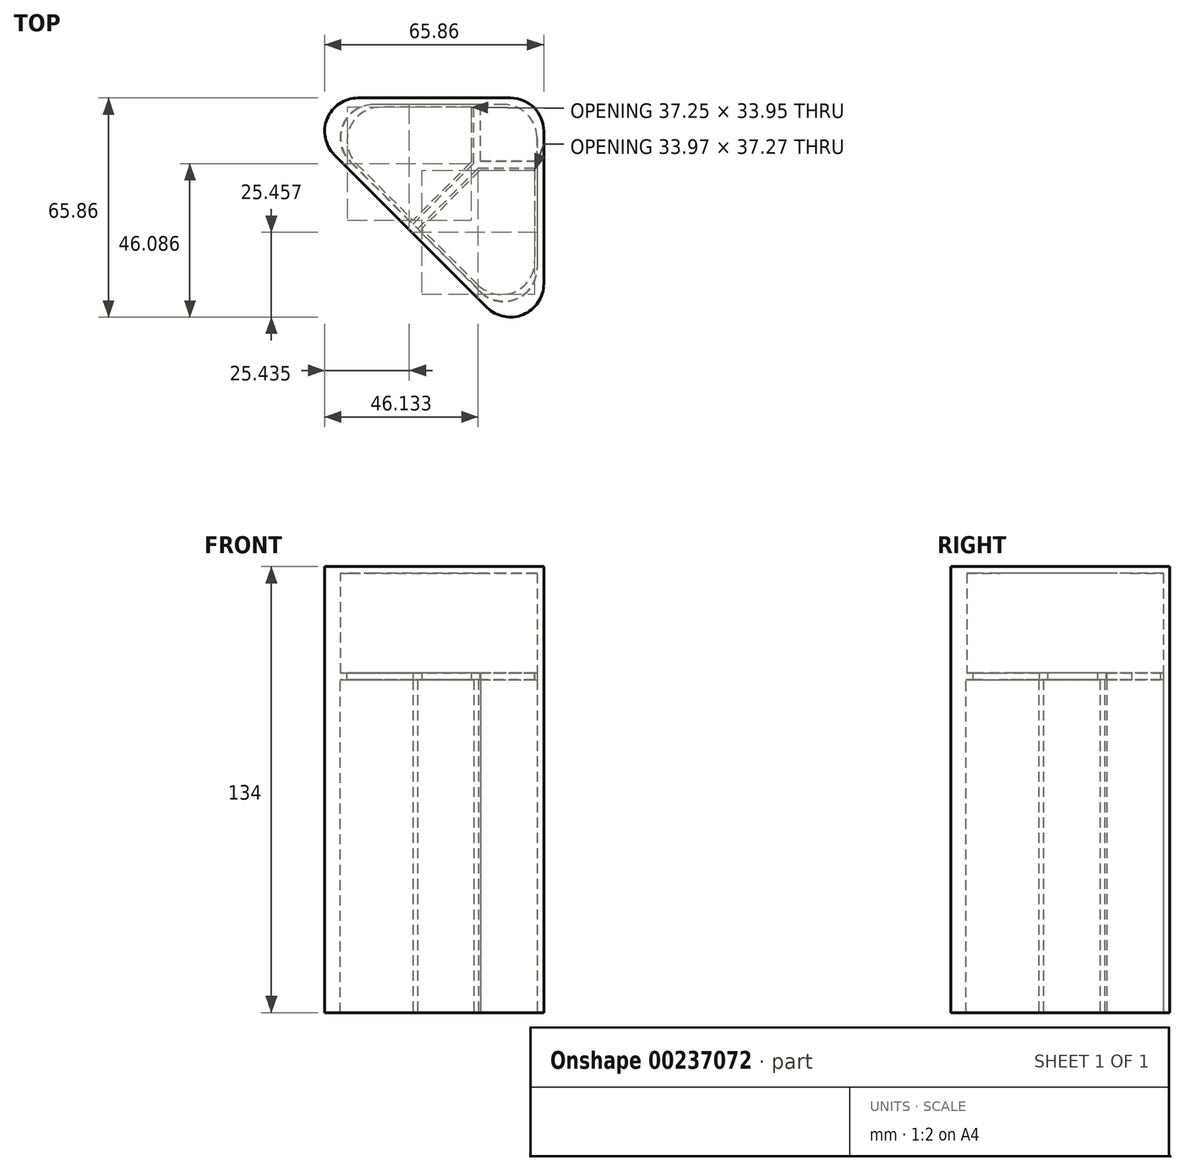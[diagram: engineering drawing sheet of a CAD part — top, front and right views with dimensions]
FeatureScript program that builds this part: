
annotation { "Feature Type Name" : "Feature", "Feature Type Description" : "" }
export const myFeature = defineFeature(function(context is Context, id is Id, definition is map)
    precondition{}
    {
        {
            var Q0;
            Q0=qCreatedBy(makeId("Top.planeOp"),FACE);
            var sketch = newSketch(context, id + "F0", { "sketchPlane" : qUnion([Q0])});
            skLineSegment(sketch, "E0.top", {"start": v(40, 40) * mm, "end": v(-40, 40) * mm});
            skLineSegment(sketch, "E0.left", {"start": v(40, -40) * mm, "end": v(40, 40) * mm});
            skPoint(sketch, "E0.middle", {"position": v(0, 0) * mm});
            skLineSegment(sketch, "E1", {"start": v(-40, 40) * mm, "end": v(40, -40) * mm});
            skPoint(sketch, "E0.bottom.end.orphan", {"position": v(-40, -40) * mm});
            skLineSegment(sketch, "E2", {"start": v(40, 40) * mm, "end": v(20, 40) * mm, "construction": true});
            skLineSegment(sketch, "E3", {"start": v(40, 40) * mm, "end": v(20, 20) * mm, "construction": true});
            skPoint(sketch, "E4.orphan", {"position": v(-20, 20) * mm});
            skPoint(sketch, "E5.orphan", {"position": v(20, -20) * mm});
            skLineSegment(sketch, "E6", {"start": v(0, 0) * mm, "end": v(-0.7, 0.7) * mm, "construction": true});
            skLineSegment(sketch, "E7", {"start": v(0.61, 2.03) * mm, "end": v(19, 20.41) * mm});
            skLineSegment(sketch, "E8", {"start": v(21, 21) * mm, "end": v(21, 38) * mm});
            skLineSegment(sketch, "E9.MirrorCS", {"start": v(19, 20.41) * mm, "end": v(19, 38) * mm});
            skPoint(sketch, "E10.start.orphan", {"position": v(20, 21.41) * mm});
            skPoint(sketch, "E11.MirrorCS.end.orphan", {"position": v(21, 20) * mm});
            skPoint(sketch, "E11.MirrorCS.start.orphan", {"position": v(40, 20) * mm});
            skLineSegment(sketch, "E12.0", {"start": v(38, 38) * mm, "end": v(21, 38) * mm});
            skLineSegment(sketch, "E13.trimOffspring", {"start": v(19, 38) * mm, "end": v(-35.36, 38) * mm});
            skLineSegment(sketch, "E14.0", {"start": v(-40.1, 39.9) * mm, "end": v(39.9, -40.1) * mm});
            skLineSegment(sketch, "E15.trimOffspring", {"start": v(-38, 38) * mm, "end": v(-38.19, 38) * mm});
            skLineSegment(sketch, "E16.trimOffspring", {"start": v(-35.36, 38) * mm, "end": v(0.61, 2.03) * mm});
            skLineSegment(sketch, "E17.trimOffspring", {"start": v(40, -37.36) * mm, "end": v(41.32, -38.68) * mm});
            skLineSegment(sketch, "E18.MirrorCS", {"start": v(38, 19) * mm, "end": v(38, -35.36) * mm});
            skLineSegment(sketch, "E19.MirrorCS", {"start": v(20.41, 19) * mm, "end": v(38, 19) * mm});
            skLineSegment(sketch, "E20.MirrorCS", {"start": v(21, 21) * mm, "end": v(38, 21) * mm});
            skLineSegment(sketch, "E21.MirrorCS", {"start": v(38, 38) * mm, "end": v(38, 21) * mm});
            skLineSegment(sketch, "E22.MirrorCS", {"start": v(2.03, 0.61) * mm, "end": v(20.41, 19) * mm});
            skLineSegment(sketch, "E23.MirrorCS", {"start": v(38, -35.36) * mm, "end": v(2.03, 0.61) * mm});
            skSolve(sketch);
        }
        {
            var Q0;
            {var subQ0=sQuery(id+"F0.wireOp",EDGE,"E0.top");Q0=makeQuery(id+"F0.imprint","IMPRINT",FACE,{"disambiguationData":[TD([[makeQuery(id+"F0.imprint","IMPRINT",EDGE,{"derivedFrom":subQ0}),1.0]])]});}
            extrude(context, id + "F1", {"entities" : qUnion([Q0]), "depth" : 100 * mm});
        }
        {
            var Q0;
            Q0=makeQuery(id+"F1.opExtrude","CAP_FACE",FACE,{"disambiguationData":[OSD([sQuery(id+"F0.wireOp",EDGE,"E0.top"),sQuery(id+"F0.wireOp",EDGE,"E0.left"),sQuery(id+"F0.wireOp",EDGE,"E1"),sQuery(id+"F0.wireOp",EDGE,"E7"),sQuery(id+"F0.wireOp",EDGE,"E8"),sQuery(id+"F0.wireOp",EDGE,"E9.MirrorCS"),sQuery(id+"F0.wireOp",EDGE,"E12.0"),sQuery(id+"F0.wireOp",EDGE,"E13.trimOffspring"),sQuery(id+"F0.wireOp",EDGE,"E16.trimOffspring"),sQuery(id+"F0.wireOp",EDGE,"E18.MirrorCS"),sQuery(id+"F0.wireOp",EDGE,"E19.MirrorCS"),sQuery(id+"F0.wireOp",EDGE,"E20.MirrorCS"),sQuery(id+"F0.wireOp",EDGE,"E21.MirrorCS"),sQuery(id+"F0.wireOp",EDGE,"E22.MirrorCS"),sQuery(id+"F0.wireOp",EDGE,"E23.MirrorCS")])],"isStart":false});
            cPlane(context, id + "F2", {"entities" : qUnion([Q0]), "cplaneType" : CPlaneType.OFFSET, "offset" : 0 * mm, "width" : 150 * mm, "height" : 150 * mm});
        }
        {
            var Q0;
            Q0=qCreatedBy(id+"F2.planeOp",FACE);
            var sketch = newSketch(context, id + "F3", { "sketchPlane" : qUnion([Q0])});
            skLineSegment(sketch, "E24.0", {"start": v(-40, 40) * mm, "end": v(0, 0) * mm});
            skLineSegment(sketch, "E25.0", {"start": v(40, 40) * mm, "end": v(-40, 40) * mm});
            skLineSegment(sketch, "E26.0", {"start": v(21, 21) * mm, "end": v(21, 38) * mm});
            skLineSegment(sketch, "E27", {"start": v(21, 38) * mm, "end": v(21, 21) * mm});
            skLineSegment(sketch, "E28", {"start": v(1.98, 1.98) * mm, "end": v(0, 0) * mm});
            skLineSegment(sketch, "E29.0", {"start": v(-33.24, 37.2) * mm, "end": v(0.7, 3.25) * mm});
            skLineSegment(sketch, "E30.0", {"start": v(18.2, 20.75) * mm, "end": v(0.7, 3.25) * mm});
            skLineSegment(sketch, "E31.0", {"start": v(18.2, 37.2) * mm, "end": v(18.2, 21) * mm});
            skLineSegment(sketch, "E32", {"start": v(18.2, 21) * mm, "end": v(18.2, 20.75) * mm});
            skLineSegment(sketch, "E33.trimOffspring", {"start": v(18.2, 37.2) * mm, "end": v(-33.24, 37.2) * mm});
            skLineSegment(sketch, "E34", {"start": v(21, 38) * mm, "end": v(37.97, 38) * mm});
            skLineSegment(sketch, "E35", {"start": v(37.97, 38) * mm, "end": v(21, 21) * mm, "construction": true});
            skPoint(sketch, "E36.0.start.orphan", {"position": v(40, -40) * mm});
            skLineSegment(sketch, "E37.MirrorCS", {"start": v(38, 21.03) * mm, "end": v(21, 21) * mm});
            skLineSegment(sketch, "E38.MirrorCS", {"start": v(38, 21.03) * mm, "end": v(37.97, 38) * mm});
            skLineSegment(sketch, "E39.MirrorCS", {"start": v(37.2, 18.23) * mm, "end": v(21, 18.2) * mm});
            skLineSegment(sketch, "E40.MirrorCS", {"start": v(37.2, 18.23) * mm, "end": v(37.3, -33.2) * mm});
            skLineSegment(sketch, "E41.MirrorCS", {"start": v(20.75, 18.2) * mm, "end": v(3.3, 0.67) * mm});
            skLineSegment(sketch, "E42.MirrorCS", {"start": v(21, 18.2) * mm, "end": v(20.75, 18.2) * mm});
            skLineSegment(sketch, "E43.MirrorCS", {"start": v(37.3, -33.2) * mm, "end": v(3.3, 0.67) * mm});
            skLineSegment(sketch, "E44", {"start": v(0, 0) * mm, "end": v(40, -40) * mm});
            skLineSegment(sketch, "E45", {"start": v(40, 40) * mm, "end": v(40, -40) * mm});
            skSolve(sketch);
        }
        {
            var Q0;
            Q0=makeQuery(id+"F3.imprint","IMPRINT",FACE,{"disambiguationData":[TD([[makeQuery(id+"F3.imprint","IMPRINT",EDGE,{"derivedFrom":sQuery(id+"F3.wireOp",EDGE,"E24.0")}),1.0]])]});
            extrude(context, id + "F4", {"entities" : qUnion([Q0]), "operationType" : NewBodyOperationType.ADD, "depth" : 2 * mm});
        }
        {
            var Q0;
            Q0=makeQuery(id+"F4.opExtrude","CAP_FACE",FACE,{"disambiguationData":[OSD([sQuery(id+"F3.wireOp",EDGE,"E24.0"),sQuery(id+"F3.wireOp",EDGE,"E25.0"),sQuery(id+"F3.wireOp",EDGE,"E27"),sQuery(id+"F3.wireOp",EDGE,"E29.0"),sQuery(id+"F3.wireOp",EDGE,"E30.0"),sQuery(id+"F3.wireOp",EDGE,"E31.0"),sQuery(id+"F3.wireOp",EDGE,"E32"),sQuery(id+"F3.wireOp",EDGE,"E33.trimOffspring"),sQuery(id+"F3.wireOp",EDGE,"E34"),sQuery(id+"F3.wireOp",EDGE,"E37.MirrorCS"),sQuery(id+"F3.wireOp",EDGE,"E38.MirrorCS"),sQuery(id+"F3.wireOp",EDGE,"E40.MirrorCS"),sQuery(id+"F3.wireOp",EDGE,"E41.MirrorCS"),sQuery(id+"F3.wireOp",EDGE,"E39.MirrorCS"),sQuery(id+"F3.wireOp",EDGE,"E42.MirrorCS"),sQuery(id+"F3.wireOp",EDGE,"E43.MirrorCS"),sQuery(id+"F3.wireOp",EDGE,"E44"),sQuery(id+"F3.wireOp",EDGE,"E45")])],"isStart":false});
            cPlane(context, id + "F5", {"entities" : qUnion([Q0]), "cplaneType" : CPlaneType.OFFSET, "offset" : 0 * mm, "width" : 150 * mm, "height" : 150 * mm});
        }
        {
            var Q0;
            Q0=qCreatedBy(id+"F5.planeOp",FACE);
            var sketch = newSketch(context, id + "F6", { "sketchPlane" : qUnion([Q0])});
            skLineSegment(sketch, "E46.0", {"start": v(40, 40) * mm, "end": v(-40, 40) * mm});
            skLineSegment(sketch, "E47.0", {"start": v(-40, 40) * mm, "end": v(40, -40) * mm});
            skLineSegment(sketch, "E48.0", {"start": v(40, 40) * mm, "end": v(40, -40) * mm});
            skLineSegment(sketch, "E49.0", {"start": v(38, 38) * mm, "end": v(-35.17, 38) * mm});
            skLineSegment(sketch, "E49.1", {"start": v(38, 38) * mm, "end": v(38, -35.17) * mm});
            skLineSegment(sketch, "E49.2", {"start": v(-35.17, 38) * mm, "end": v(38, -35.17) * mm});
            skSolve(sketch);
        }
        {
            var Q0;
            Q0 = qSketchRegion(id + "F6", true);
            extrude(context, id + "F7", {"entities" : qUnion([Q0]), "operationType" : NewBodyOperationType.ADD, "depth" : 30 * mm});
        }
        {
            var Q0;
            Q0=makeQuery(id+"F7.opExtrude","CAP_FACE",FACE,{"disambiguationData":[OSD([sQuery(id+"F6.wireOp",EDGE,"E46.0"),sQuery(id+"F6.wireOp",EDGE,"E47.0"),sQuery(id+"F6.wireOp",EDGE,"E48.0"),sQuery(id+"F6.wireOp",EDGE,"E49.0"),sQuery(id+"F6.wireOp",EDGE,"E49.1"),sQuery(id+"F6.wireOp",EDGE,"E49.2")])],"isStart":false});
            cPlane(context, id + "F8", {"entities" : qUnion([Q0]), "cplaneType" : CPlaneType.OFFSET, "offset" : 0 * mm, "width" : 150 * mm, "height" : 150 * mm});
        }
        {
            var Q0;
            Q0=qCreatedBy(id+"F8.planeOp",FACE);
            var sketch = newSketch(context, id + "F9", { "sketchPlane" : qUnion([Q0])});
            skLineSegment(sketch, "E50.0", {"start": v(40, 40) * mm, "end": v(-40, 40) * mm});
            skLineSegment(sketch, "E51.0", {"start": v(-40, 40) * mm, "end": v(40, -40) * mm});
            skLineSegment(sketch, "E52.0", {"start": v(40, 40) * mm, "end": v(40, -40) * mm});
            skSolve(sketch);
        }
        {
            var Q0;
            Q0 = qSketchRegion(id + "F9", true);
            extrude(context, id + "F10", {"entities" : qUnion([Q0]), "operationType" : NewBodyOperationType.ADD, "depth" : 2 * mm});
        }
        {
            var Q0;
            Q0=makeQuery(id+"F1.opExtrude","SWEPT_EDGE",EDGE,{"disambiguationData":[OSD([sQuery(id+"F0.wireOp",EDGE,"E13.trimOffspring"),sQuery(id+"F0.wireOp",EDGE,"E16.trimOffspring")])]});
            var Q1;
            Q1=makeQuery(id+"F4.opExtrude","SWEPT_EDGE",EDGE,{"disambiguationData":[OSD([sQuery(id+"F3.wireOp",EDGE,"E29.0"),sQuery(id+"F3.wireOp",EDGE,"E33.trimOffspring")])]});
            var Q2;
            Q2=makeQuery(id+"F7.opExtrude","SWEPT_EDGE",EDGE,{"disambiguationData":[OSD([sQuery(id+"F6.wireOp",EDGE,"E49.0"),sQuery(id+"F6.wireOp",EDGE,"E49.2")])]});
            var Q3;
            Q3=makeQuery(id+"F10.boolean.opBoolean","MERGE",EDGE,{"derivedFrom":[makeQuery(id+"F7.boolean.opBoolean","MERGE",EDGE,{"derivedFrom":[makeQuery(id+"F4.boolean.opBoolean","MERGE",EDGE,{"derivedFrom":[makeQuery(id+"F1.opExtrude","SWEPT_EDGE",EDGE,{"disambiguationData":[OSD([sQuery(id+"F0.wireOp",EDGE,"E0.top"),sQuery(id+"F0.wireOp",EDGE,"E1")])]}),makeQuery(id+"F4.opExtrude","SWEPT_EDGE",EDGE,{"disambiguationData":[OSD([sQuery(id+"F3.wireOp",EDGE,"E24.0"),sQuery(id+"F3.wireOp",EDGE,"E25.0")])]})]}),makeQuery(id+"F7.opExtrude","SWEPT_EDGE",EDGE,{"disambiguationData":[OSD([sQuery(id+"F6.wireOp",EDGE,"E46.0"),sQuery(id+"F6.wireOp",EDGE,"E47.0")])]})]}),makeQuery(id+"F10.opExtrude","SWEPT_EDGE",EDGE,{"disambiguationData":[OSD([sQuery(id+"F9.wireOp",EDGE,"E50.0"),sQuery(id+"F9.wireOp",EDGE,"E51.0")])]})]});
            var Q4;
            Q4=makeQuery(id+"F1.opExtrude","SWEPT_EDGE",EDGE,{"disambiguationData":[OSD([sQuery(id+"F0.wireOp",EDGE,"E18.MirrorCS"),sQuery(id+"F0.wireOp",EDGE,"E23.MirrorCS")])]});
            var Q5;
            Q5=makeQuery(id+"F10.boolean.opBoolean","MERGE",EDGE,{"derivedFrom":[makeQuery(id+"F7.boolean.opBoolean","MERGE",EDGE,{"derivedFrom":[makeQuery(id+"F4.boolean.opBoolean","MERGE",EDGE,{"derivedFrom":[makeQuery(id+"F1.opExtrude","SWEPT_EDGE",EDGE,{"disambiguationData":[OSD([sQuery(id+"F0.wireOp",EDGE,"E0.left"),sQuery(id+"F0.wireOp",EDGE,"E1")])]}),makeQuery(id+"F4.opExtrude","SWEPT_EDGE",EDGE,{"disambiguationData":[OSD([sQuery(id+"F3.wireOp",EDGE,"E44"),sQuery(id+"F3.wireOp",EDGE,"E45")])]})]}),makeQuery(id+"F7.opExtrude","SWEPT_EDGE",EDGE,{"disambiguationData":[OSD([sQuery(id+"F6.wireOp",EDGE,"E47.0"),sQuery(id+"F6.wireOp",EDGE,"E48.0")])]})]}),makeQuery(id+"F10.opExtrude","SWEPT_EDGE",EDGE,{"disambiguationData":[OSD([sQuery(id+"F9.wireOp",EDGE,"E51.0"),sQuery(id+"F9.wireOp",EDGE,"E52.0")])]})]});
            var Q6;
            Q6=makeQuery(id+"F4.opExtrude","SWEPT_EDGE",EDGE,{"disambiguationData":[OSD([sQuery(id+"F3.wireOp",EDGE,"E40.MirrorCS"),sQuery(id+"F3.wireOp",EDGE,"E43.MirrorCS")])]});
            var Q7;
            Q7=makeQuery(id+"F7.opExtrude","SWEPT_EDGE",EDGE,{"disambiguationData":[OSD([sQuery(id+"F6.wireOp",EDGE,"E49.1"),sQuery(id+"F6.wireOp",EDGE,"E49.2")])]});
            var Q8;
            Q8=makeQuery(id+"F1.opExtrude","SWEPT_EDGE",EDGE,{"disambiguationData":[OSD([sQuery(id+"F0.wireOp",EDGE,"E12.0"),sQuery(id+"F0.wireOp",EDGE,"E21.MirrorCS")])]});
            var Q9;
            Q9=makeQuery(id+"F10.boolean.opBoolean","MERGE",EDGE,{"derivedFrom":[makeQuery(id+"F7.boolean.opBoolean","MERGE",EDGE,{"derivedFrom":[makeQuery(id+"F4.boolean.opBoolean","MERGE",EDGE,{"derivedFrom":[makeQuery(id+"F1.opExtrude","SWEPT_EDGE",EDGE,{"disambiguationData":[OSD([sQuery(id+"F0.wireOp",EDGE,"E0.top"),sQuery(id+"F0.wireOp",EDGE,"E0.left")])]}),makeQuery(id+"F4.opExtrude","SWEPT_EDGE",EDGE,{"disambiguationData":[OSD([sQuery(id+"F3.wireOp",EDGE,"E25.0"),sQuery(id+"F3.wireOp",EDGE,"E45")])]})]}),makeQuery(id+"F7.opExtrude","SWEPT_EDGE",EDGE,{"disambiguationData":[OSD([sQuery(id+"F6.wireOp",EDGE,"E46.0"),sQuery(id+"F6.wireOp",EDGE,"E48.0")])]})]}),makeQuery(id+"F10.opExtrude","SWEPT_EDGE",EDGE,{"disambiguationData":[OSD([sQuery(id+"F9.wireOp",EDGE,"E50.0"),sQuery(id+"F9.wireOp",EDGE,"E52.0")])]})]});
            fillet(context, id + "F11", {"entities" : qUnion([Q0, Q1, Q2, Q3, Q4, Q5, Q6, Q7, Q8, Q9]), "radius" : 10 * mm, "tangentPropagation" : true, "allowEdgeOverflow" : false});
        }
    });
